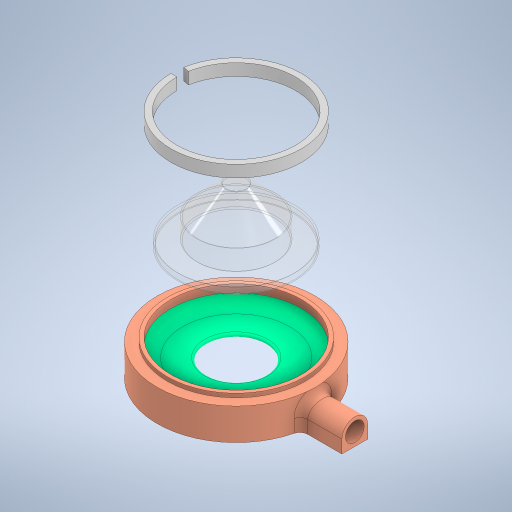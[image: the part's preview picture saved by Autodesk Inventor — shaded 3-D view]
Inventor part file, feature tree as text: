
AUTODESK INVENTOR PART (.ipt)
format: ipt  version: 2023.3 (Build 273359000, 359)  size: 1,068,032 bytes
history: native  units: mm
features: other x18, sketch x6, extrude x6, move_body x6, boolean_combine x4, thicken_offset x4, direct_edit x3, emboss x2, projected_geometry x2
ambient origin geometry x8: Origin, YZ Plane, XZ Plane, XY Plane, X Axis, Y Axis, Z Axis, Center Point
bodies: Solid3 (feature_tree), Solid4 (feature_tree), Solid8 (feature_tree), Solid9 (feature_tree), Solid1 (feature_tree), Solid1_1 (feature_tree), Solid1_2 (feature_tree), Solid1_3 (feature_tree), Solid1_4 (feature_tree), Solid1_5 (feature_tree), Solid1_6 (feature_tree)
feature tree (51):
  other  "Sealingring_holder.ipt"
  other  "Sealingring.ipt"
  other  "FEP_foil.ipt"
  other  "FEP_foil_clip_ring.ipt"
  sketch  "Sketch1"  dims[d0=10.0mm d1=10.0mm]
  extrude  "Extrusion1"  Depth=10.0mm
  boolean_combine  "Combine1"
  sketch  "Sketch2"  dims[d2=8.0mm d3=0.0mm d4=8.8mm]
  extrude  "Extrusion2"  Depth=8.8mm
  thicken_offset  "Thicken1"
  extrude  "Extrusion3"  Depth=0.1mm
  boolean_combine  "Combine2"
  extrude  "Extrusion4"  Depth=8.0mm TaperAngle=0.0deg
  thicken_offset  "Thicken2"
  thicken_offset  "Thicken3"
  thicken_offset  "Thicken4"
  emboss  "Emboss1"
  emboss  "Emboss2"
  extrude  "Extrusion5"  Depth=10.0mm
  boolean_combine  "Combine3"
  extrude  "Extrusion6"  Depth=10.0mm
  boolean_combine  "Combine4"
  direct_edit  "Direct Edit1"
  direct_edit  "Direct Edit2"
  direct_edit  "Direct Edit3"
  other  "Solid1::Sealingring_holder.ipt"
  other  "TaggingFeature1"
  other  "Solid1::Sealingring.ipt"
  other  "TaggingFeature2"
  other  "Solid1::Sealingring_holder.ipt_1"
  other  "TaggingFeature3"
  other  "Solid1::Sealingring.ipt_1"
  other  "TaggingFeature4"
  sketch  "Sketch3"  dims[d5=1.5mm d6=0.0mm d7=0.1mm]
  sketch  "Sketch4"  dims[d8=0.1mm d9=8.0mm d10=0.0mm]
  other  "Solid1::Sealingring_holder.ipt_2"
  other  "TaggingFeature5"
  sketch  "Sketch5"  dims[d11=10.0mm d12=10.0mm]
  projected_geometry  "Projected Loop1"
  projected_geometry  "Projected Loop2"
  sketch  "Sketch6"  dims[d13=3.0mm d14=-1.22173mm d15=0.341181mm d16=0.35mm d17=0.1mm d18=0.1mm d19=4.0mm d20=4.0mm d21=4.0mm d22=4.0mm d23=0.3mm d24=0.0mm d25=0.3mm d26=0.0mm d27=10.0mm d28=10.0mm d29=0.0mm d30=6.0mm d31=0.0mm d32=0.0mm d33=0.0mm d34=38.0mm d35=0.0mm d36=0.0mm d37=30.25mm d44=0.0mm d45=0.0mm d46=5.0mm d47=0.0mm d48=0.0mm d49=-12.75mm d50=10.0mm d51=5.416869mm d52=-63.998605mm d53=-26.5mm d54=10.0mm d55=0.0mm d56=0.0mm d57=51.5mm]
  other  "Solid1::FEP_foil.ipt"
  other  "TaggingFeature6"
  other  "Solid1::FEP_foil_clip_ring.ipt"
  other  "TaggingFeature7"
  move_body  "Move1"
  move_body  "Move2"
  move_body  "Move5"
  move_body  "Move6"
  move_body  "Move7"
  move_body  "Move8"
